# Revit family: Plumbing_Fixtures-Oasis-Drinking_Fountain_HD_Vandal_Resistant_Single
name_source: partatom
category: Plumbing Fixtures
units: mm (PartAtom-declared; Revit-internal decimal feet)

## family parameters
Cut with Voids When Loaded = Yes
Host = Face
OmniClass Number = 23.65.70.14.11
OmniClass Title = Drinking Fountains/Coolers
Part Type = Normal
Room Calculation Point = No
Round Connector Dimension = Use Diameter
Shared = No

## types (2) — shared parameters
Accessory Material = Plastic - Oasis International - Gray
Assembly Code = D2010800
Cabinet Finish = Metal - Oasis International - Brushed Stainless Steel
Cold Water Connection Diameter = 0"
Default Elevation = 1' - 1 9/32"
Depth = 1' - 7"
Filter Option = Option to add Filtration
Finish = Metal - Oasis International - Brushed Stainless Steel
Flow Rate = 8 GPH
Frequency = 60 Hz
Height = 1' - 6 29/32"
Instruction Sheet Link = https://www.oasiscoolers.com
Keynote = 22 40 00.A1
Load Classification = Power
Manufacturer = OASIS International
Manufacturer Fax Number = 1-(614) 322-2529
Product Documentation Link = https://www.oasiscoolers.com
Product Page URL = https://www.oasiscoolers.com
URL = https://www.oasiscoolers.com
Version = 2021 - v1.0a
Voltage = 115 V
Voltage Comment = 115 Volts, 60 Hz
Warranty URL = https://www.oasiscoolers.com
Waste Water Connection Diameter = 0' - 1 1/4"
Water Pressure = 60.00 psi
Water Pressure Range = 20 - 100 PSI
Width = 1' - 5 3/4"

## per-type parameters (varying)
| type | Chilling Option | Description | Full Load Current | Model | Product Name | Rated Watts | Weight |
| PGV8AC-14G-STL | Delivers 8.0 gallons of chilled drinking water per hour | Refrigerated Fountain | 5 A | PGV8AC-14G 504519 | Heavy Duty, Vandal Resistant Versacooler II, Refrigerated | 460 W | 75.00 lb |
| PGVAC-14G-STL | Non-Refrigerated Fountain | Non-Refrigerated Fountain | 0 A | PGVAC-14G 504539 | Heavy Duty, Vandal Resistant Versacooler II, Non-Refrigerated | 0 W | 42.00 lb |

## geometry (parser evidence)
native form markers: Sweep x2
no freeform markers — native parametric forms only
